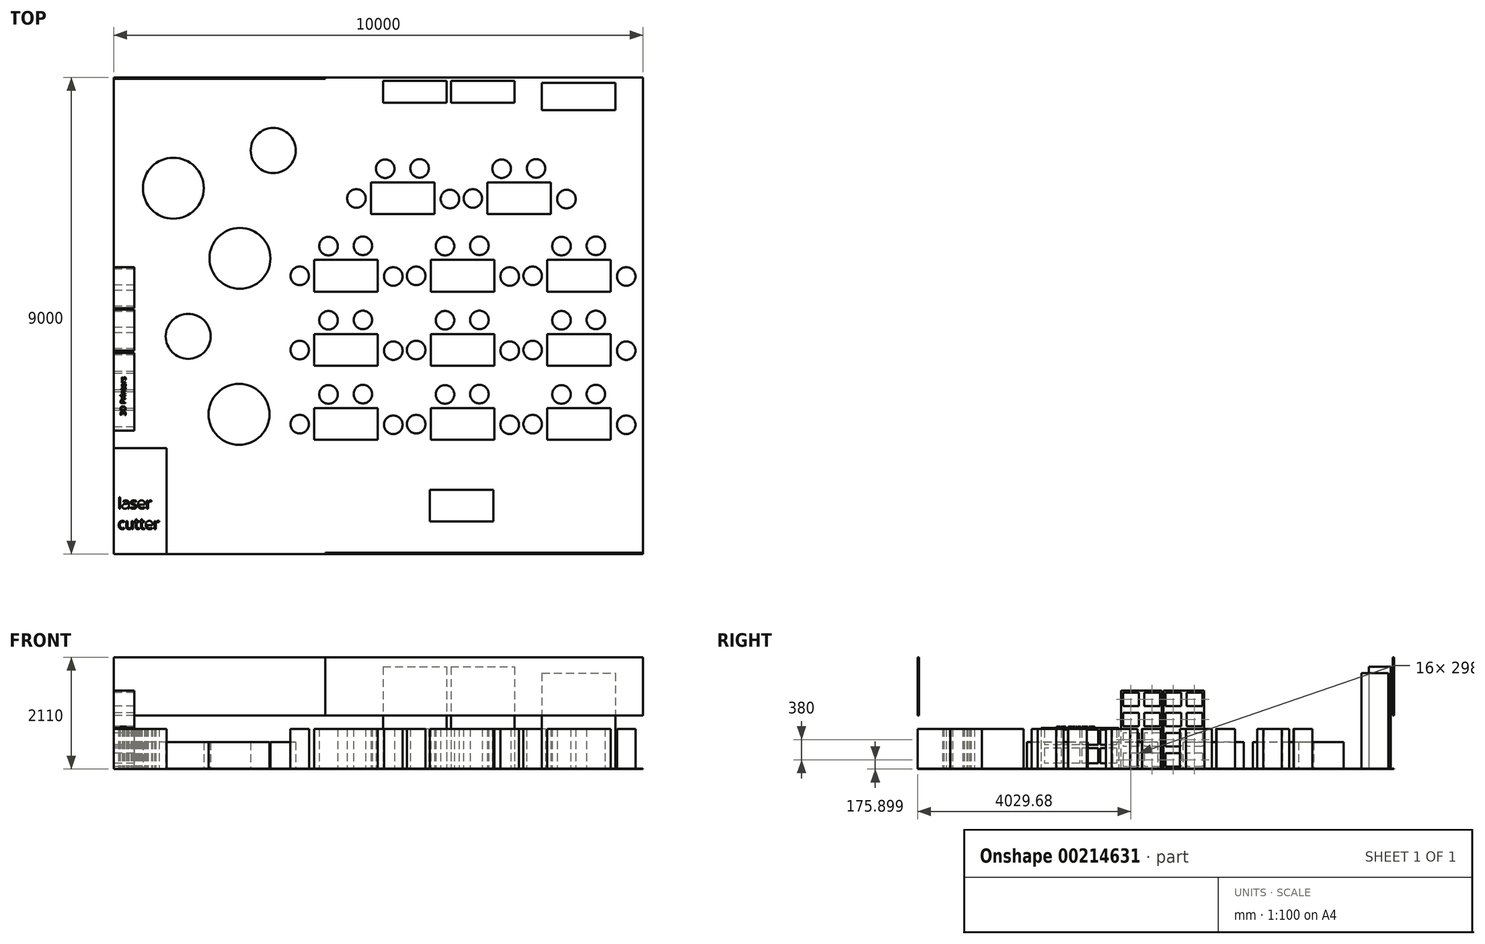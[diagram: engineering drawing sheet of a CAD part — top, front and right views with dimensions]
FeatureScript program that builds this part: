
annotation { "Feature Type Name" : "Feature", "Feature Type Description" : "" }
export const myFeature = defineFeature(function(context is Context, id is Id, definition is map)
    precondition{}
    {
        {
            var Q0;
            Q0=qCreatedBy(makeId("Top.planeOp"),FACE);
            var sketch = newSketch(context, id + "F0", { "sketchPlane" : qUnion([Q0])});
            skLineSegment(sketch, "E0.bottom", {"start": v(-5000, 4500) * mm, "end": v(5000, 4500) * mm});
            skLineSegment(sketch, "E0.top", {"start": v(-5000, -4500) * mm, "end": v(5000, -4500) * mm});
            skLineSegment(sketch, "E0.left", {"start": v(-5000, 4500) * mm, "end": v(-5000, -4500) * mm});
            skLineSegment(sketch, "E0.right", {"start": v(5000, 4500) * mm, "end": v(5000, -4500) * mm});
            skSolve(sketch);
        }
        {
            var Q0;
            Q0=makeQuery(id+"F0.imprint","IMPRINT",FACE,{"disambiguationData":[TD([[makeQuery(id+"F0.imprint","IMPRINT",EDGE,{"derivedFrom":sQuery(id+"F0.wireOp",EDGE,"E0.bottom")}),-1.0]])]});
            extrude(context, id + "F1", {"entities" : qUnion([Q0]), "oppositeDirection" : true, "depth" : 10 * mm});
        }
        {
            var Q0;
            Q0=qCreatedBy(makeId("Top.planeOp"),FACE);
            var sketch = newSketch(context, id + "F2", { "sketchPlane" : qUnion([Q0])});
            skLineSegment(sketch, "E1.bottom", {"start": v(972.24, -3285.08) * mm, "end": v(2172.24, -3285.08) * mm});
            skLineSegment(sketch, "E1.top", {"start": v(972.24, -3885.08) * mm, "end": v(2172.24, -3885.08) * mm});
            skLineSegment(sketch, "E1.left", {"start": v(972.24, -3285.08) * mm, "end": v(972.24, -3885.08) * mm});
            skLineSegment(sketch, "E1.right", {"start": v(2172.24, -3285.08) * mm, "end": v(2172.24, -3885.08) * mm});
            skLineSegment(sketch, "E2.bottom", {"start": v(3189.93, -1743.91) * mm, "end": v(4389.93, -1743.91) * mm});
            skLineSegment(sketch, "E2.top", {"start": v(3189.93, -2343.91) * mm, "end": v(4389.93, -2343.91) * mm});
            skLineSegment(sketch, "E2.left", {"start": v(3189.93, -1743.91) * mm, "end": v(3189.93, -2343.91) * mm});
            skLineSegment(sketch, "E2.right", {"start": v(4389.93, -1743.91) * mm, "end": v(4389.93, -2343.91) * mm});
            skCircle(sketch, "E3", {"center": v(2914.35, -2047.3) * mm, "radius": 175 * mm});
            skCircle(sketch, "E4", {"center": v(4108.01, -1479.73) * mm, "radius": 175 * mm});
            skCircle(sketch, "E5", {"center": v(3458.52, -1485.58) * mm, "radius": 175 * mm});
            skCircle(sketch, "E6", {"center": v(4681.44, -2059) * mm, "radius": 175 * mm});
            skCircle(sketch, "E7.0.1.0", {"center": v(2914.35, -647.3) * mm, "radius": 175 * mm});
            skCircle(sketch, "E7.0.1.1", {"center": v(4681.44, -659) * mm, "radius": 175 * mm});
            skLineSegment(sketch, "E7.0.1.2", {"start": v(4389.93, -343.91) * mm, "end": v(4389.93, -943.91) * mm});
            skCircle(sketch, "E7.0.1.3", {"center": v(3458.52, -85.58) * mm, "radius": 175 * mm});
            skLineSegment(sketch, "E7.0.1.4", {"start": v(3189.93, -343.91) * mm, "end": v(3189.93, -943.91) * mm});
            skCircle(sketch, "E7.0.1.5", {"center": v(4108.01, -79.73) * mm, "radius": 175 * mm});
            skLineSegment(sketch, "E7.0.1.6", {"start": v(3189.93, -943.91) * mm, "end": v(4389.93, -943.91) * mm});
            skLineSegment(sketch, "E7.0.1.7", {"start": v(3189.93, -343.91) * mm, "end": v(4389.93, -343.91) * mm});
            skCircle(sketch, "E7.0.2.0", {"center": v(2914.35, 752.7) * mm, "radius": 175 * mm});
            skCircle(sketch, "E7.0.2.1", {"center": v(4681.44, 741) * mm, "radius": 175 * mm});
            skLineSegment(sketch, "E7.0.2.2", {"start": v(4389.93, 1056.09) * mm, "end": v(4389.93, 456.09) * mm});
            skCircle(sketch, "E7.0.2.3", {"center": v(3458.52, 1314.42) * mm, "radius": 175 * mm});
            skLineSegment(sketch, "E7.0.2.4", {"start": v(3189.93, 1056.09) * mm, "end": v(3189.93, 456.09) * mm});
            skCircle(sketch, "E7.0.2.5", {"center": v(4108.01, 1320.27) * mm, "radius": 175 * mm});
            skLineSegment(sketch, "E7.0.2.6", {"start": v(3189.93, 456.09) * mm, "end": v(4389.93, 456.09) * mm});
            skLineSegment(sketch, "E7.0.2.7", {"start": v(3189.93, 1056.09) * mm, "end": v(4389.93, 1056.09) * mm});
            skCircle(sketch, "E7.1.0.0", {"center": v(714.35, -2047.3) * mm, "radius": 175 * mm});
            skCircle(sketch, "E7.1.0.1", {"center": v(2481.44, -2059) * mm, "radius": 175 * mm});
            skLineSegment(sketch, "E7.1.0.2", {"start": v(2189.93, -1743.91) * mm, "end": v(2189.93, -2343.91) * mm});
            skCircle(sketch, "E7.1.0.3", {"center": v(1258.52, -1485.58) * mm, "radius": 175 * mm});
            skLineSegment(sketch, "E7.1.0.4", {"start": v(989.93, -1743.91) * mm, "end": v(989.93, -2343.91) * mm});
            skCircle(sketch, "E7.1.0.5", {"center": v(1908.01, -1479.73) * mm, "radius": 175 * mm});
            skLineSegment(sketch, "E7.1.0.6", {"start": v(989.93, -2343.91) * mm, "end": v(2189.93, -2343.91) * mm});
            skLineSegment(sketch, "E7.1.0.7", {"start": v(989.93, -1743.91) * mm, "end": v(2189.93, -1743.91) * mm});
            skCircle(sketch, "E7.1.1.0", {"center": v(714.35, -647.3) * mm, "radius": 175 * mm});
            skCircle(sketch, "E7.1.1.1", {"center": v(2481.44, -659) * mm, "radius": 175 * mm});
            skLineSegment(sketch, "E7.1.1.2", {"start": v(2189.93, -343.91) * mm, "end": v(2189.93, -943.91) * mm});
            skCircle(sketch, "E7.1.1.3", {"center": v(1258.52, -85.58) * mm, "radius": 175 * mm});
            skLineSegment(sketch, "E7.1.1.4", {"start": v(989.93, -343.91) * mm, "end": v(989.93, -943.91) * mm});
            skCircle(sketch, "E7.1.1.5", {"center": v(1908.01, -79.73) * mm, "radius": 175 * mm});
            skLineSegment(sketch, "E7.1.1.6", {"start": v(989.93, -943.91) * mm, "end": v(2189.93, -943.91) * mm});
            skLineSegment(sketch, "E7.1.1.7", {"start": v(989.93, -343.91) * mm, "end": v(2189.93, -343.91) * mm});
            skCircle(sketch, "E7.1.2.0", {"center": v(714.35, 752.7) * mm, "radius": 175 * mm});
            skCircle(sketch, "E7.1.2.1", {"center": v(2481.44, 741) * mm, "radius": 175 * mm});
            skLineSegment(sketch, "E7.1.2.2", {"start": v(2189.93, 1056.09) * mm, "end": v(2189.93, 456.09) * mm});
            skCircle(sketch, "E7.1.2.3", {"center": v(1258.52, 1314.42) * mm, "radius": 175 * mm});
            skLineSegment(sketch, "E7.1.2.4", {"start": v(989.93, 1056.09) * mm, "end": v(989.93, 456.09) * mm});
            skCircle(sketch, "E7.1.2.5", {"center": v(1908.01, 1320.27) * mm, "radius": 175 * mm});
            skLineSegment(sketch, "E7.1.2.6", {"start": v(989.93, 456.09) * mm, "end": v(2189.93, 456.09) * mm});
            skLineSegment(sketch, "E7.1.2.7", {"start": v(989.93, 1056.09) * mm, "end": v(2189.93, 1056.09) * mm});
            skCircle(sketch, "E7.2.0.0", {"center": v(-1485.65, -2047.3) * mm, "radius": 175 * mm});
            skCircle(sketch, "E7.2.0.1", {"center": v(281.44, -2059) * mm, "radius": 175 * mm});
            skLineSegment(sketch, "E7.2.0.2", {"start": v(-10.07, -1743.91) * mm, "end": v(-10.07, -2343.91) * mm});
            skCircle(sketch, "E7.2.0.3", {"center": v(-941.48, -1485.58) * mm, "radius": 175 * mm});
            skLineSegment(sketch, "E7.2.0.4", {"start": v(-1210.07, -1743.91) * mm, "end": v(-1210.07, -2343.91) * mm});
            skCircle(sketch, "E7.2.0.5", {"center": v(-291.99, -1479.73) * mm, "radius": 175 * mm});
            skLineSegment(sketch, "E7.2.0.6", {"start": v(-1210.07, -2343.91) * mm, "end": v(-10.07, -2343.91) * mm});
            skLineSegment(sketch, "E7.2.0.7", {"start": v(-1210.07, -1743.91) * mm, "end": v(-10.07, -1743.91) * mm});
            skCircle(sketch, "E7.2.1.0", {"center": v(-1485.65, -647.3) * mm, "radius": 175 * mm});
            skCircle(sketch, "E7.2.1.1", {"center": v(281.44, -659) * mm, "radius": 175 * mm});
            skLineSegment(sketch, "E7.2.1.2", {"start": v(-10.07, -343.91) * mm, "end": v(-10.07, -943.91) * mm});
            skCircle(sketch, "E7.2.1.3", {"center": v(-941.48, -85.58) * mm, "radius": 175 * mm});
            skLineSegment(sketch, "E7.2.1.4", {"start": v(-1210.07, -343.91) * mm, "end": v(-1210.07, -943.91) * mm});
            skCircle(sketch, "E7.2.1.5", {"center": v(-291.99, -79.73) * mm, "radius": 175 * mm});
            skLineSegment(sketch, "E7.2.1.6", {"start": v(-1210.07, -943.91) * mm, "end": v(-10.07, -943.91) * mm});
            skLineSegment(sketch, "E7.2.1.7", {"start": v(-1210.07, -343.91) * mm, "end": v(-10.07, -343.91) * mm});
            skCircle(sketch, "E7.2.2.0", {"center": v(-1485.65, 752.7) * mm, "radius": 175 * mm});
            skCircle(sketch, "E7.2.2.1", {"center": v(281.44, 741) * mm, "radius": 175 * mm});
            skLineSegment(sketch, "E7.2.2.2", {"start": v(-10.07, 1056.09) * mm, "end": v(-10.07, 456.09) * mm});
            skCircle(sketch, "E7.2.2.3", {"center": v(-941.48, 1314.42) * mm, "radius": 175 * mm});
            skLineSegment(sketch, "E7.2.2.4", {"start": v(-1210.07, 1056.09) * mm, "end": v(-1210.07, 456.09) * mm});
            skCircle(sketch, "E7.2.2.5", {"center": v(-291.99, 1320.27) * mm, "radius": 175 * mm});
            skLineSegment(sketch, "E7.2.2.6", {"start": v(-1210.07, 456.09) * mm, "end": v(-10.07, 456.09) * mm});
            skLineSegment(sketch, "E7.2.2.7", {"start": v(-1210.07, 1056.09) * mm, "end": v(-10.07, 1056.09) * mm});
            skLineSegment(sketch, "E7.direction1", {"start": v(3189.93, -2343.91) * mm, "end": v(989.93, -2343.91) * mm, "construction": true});
            skLineSegment(sketch, "E7.direction2", {"start": v(3189.93, -2343.91) * mm, "end": v(3189.93, -943.91) * mm, "construction": true});
            skCircle(sketch, "E8.1.2.0", {"center": v(1784.74, 2214.43) * mm, "radius": 175 * mm});
            skCircle(sketch, "E8.1.2.1", {"center": v(3551.83, 2202.73) * mm, "radius": 175 * mm});
            skLineSegment(sketch, "E8.1.2.2", {"start": v(3260.32, 2517.83) * mm, "end": v(3260.32, 1917.83) * mm});
            skCircle(sketch, "E8.1.2.3", {"center": v(2328.91, 2776.16) * mm, "radius": 175 * mm});
            skLineSegment(sketch, "E8.1.2.4", {"start": v(2060.32, 2517.83) * mm, "end": v(2060.32, 1917.83) * mm});
            skCircle(sketch, "E8.1.2.5", {"center": v(2978.4, 2782) * mm, "radius": 175 * mm});
            skLineSegment(sketch, "E8.1.2.6", {"start": v(2060.32, 1917.83) * mm, "end": v(3260.32, 1917.83) * mm});
            skLineSegment(sketch, "E8.1.2.7", {"start": v(2060.32, 2517.83) * mm, "end": v(3260.32, 2517.83) * mm});
            skCircle(sketch, "E8.2.2.0", {"center": v(-415.26, 2214.43) * mm, "radius": 175 * mm});
            skCircle(sketch, "E8.2.2.1", {"center": v(1351.83, 2202.73) * mm, "radius": 175 * mm});
            skLineSegment(sketch, "E8.2.2.2", {"start": v(1060.32, 2517.83) * mm, "end": v(1060.32, 1917.83) * mm});
            skCircle(sketch, "E8.2.2.3", {"center": v(128.91, 2776.16) * mm, "radius": 175 * mm});
            skLineSegment(sketch, "E8.2.2.4", {"start": v(-139.68, 2517.83) * mm, "end": v(-139.68, 1917.83) * mm});
            skCircle(sketch, "E8.2.2.5", {"center": v(778.4, 2782) * mm, "radius": 175 * mm});
            skLineSegment(sketch, "E8.2.2.6", {"start": v(-139.68, 1917.83) * mm, "end": v(1060.32, 1917.83) * mm});
            skLineSegment(sketch, "E8.2.2.7", {"start": v(-139.68, 2517.83) * mm, "end": v(1060.32, 2517.83) * mm});
            skSolve(sketch);
        }
        {
            var Q0;
            Q0 = qSketchRegion(id + "F2", true);
            extrude(context, id + "F3", {"entities" : qUnion([Q0]), "operationType" : NewBodyOperationType.ADD, "depth" : 750 * mm});
        }
        {
            var Q0;
            Q0=qCreatedBy(makeId("Front.planeOp"),FACE);
            cPlane(context, id + "F4", {"entities" : qUnion([Q0]), "cplaneType" : CPlaneType.OFFSET, "offset" : 4500 * mm, "width" : 150 * mm, "height" : 150 * mm});
        }
        {
            var Q0;
            Q0=qCreatedBy(id+"F4.planeOp",FACE);
            var sketch = newSketch(context, id + "F5", { "sketchPlane" : qUnion([Q0])});
            skLineSegment(sketch, "E9.bottom", {"start": v(-1000, 2100) * mm, "end": v(5000, 2100) * mm});
            skLineSegment(sketch, "E9.top", {"start": v(-1000, 1000) * mm, "end": v(5000, 1000) * mm});
            skLineSegment(sketch, "E9.left", {"start": v(-1000, 2100) * mm, "end": v(-1000, 1000) * mm});
            skLineSegment(sketch, "E9.right", {"start": v(5000, 2100) * mm, "end": v(5000, 1000) * mm});
            skSolve(sketch);
        }
        {
            var Q0;
            Q0 = qSketchRegion(id + "F5", true);
            extrude(context, id + "F6", {"entities" : qUnion([Q0]), "oppositeDirection" : true, "depth" : 25 * mm});
        }
        {
            var Q0;
            Q0=qCreatedBy(makeId("Front.planeOp"),FACE);
            cPlane(context, id + "F7", {"entities" : qUnion([Q0]), "cplaneType" : CPlaneType.OFFSET, "offset" : 4500 * mm, "oppositeDirection" : true, "width" : 150 * mm, "height" : 150 * mm});
        }
        {
            var Q0;
            Q0=qCreatedBy(makeId("Top.planeOp"),FACE);
            var sketch = newSketch(context, id + "F8", { "sketchPlane" : qUnion([Q0])});
            skLineSegment(sketch, "E10.bottom", {"start": v(86.82, 4433.97) * mm, "end": v(1286.82, 4433.97) * mm});
            skLineSegment(sketch, "E10.top", {"start": v(86.82, 4023.97) * mm, "end": v(1286.82, 4023.97) * mm});
            skLineSegment(sketch, "E10.left", {"start": v(86.82, 4433.97) * mm, "end": v(86.82, 4023.97) * mm});
            skLineSegment(sketch, "E10.right", {"start": v(1286.82, 4433.97) * mm, "end": v(1286.82, 4023.97) * mm});
            skLineSegment(sketch, "E11.bottom", {"start": v(1369.44, 4433.5) * mm, "end": v(2569.44, 4433.5) * mm});
            skLineSegment(sketch, "E11.top", {"start": v(1369.44, 4023.5) * mm, "end": v(2569.44, 4023.5) * mm});
            skLineSegment(sketch, "E11.left", {"start": v(1369.44, 4433.5) * mm, "end": v(1369.44, 4023.5) * mm});
            skLineSegment(sketch, "E11.right", {"start": v(2569.44, 4433.5) * mm, "end": v(2569.44, 4023.5) * mm});
            skSolve(sketch);
        }
        {
            var Q0;
            Q0 = qSketchRegion(id + "F8", true);
            extrude(context, id + "F9", {"entities" : qUnion([Q0]), "operationType" : NewBodyOperationType.ADD, "depth" : 1920 * mm});
        }
        {
            var Q0;
            Q0=qCreatedBy(makeId("Top.planeOp"),FACE);
            var sketch = newSketch(context, id + "F10", { "sketchPlane" : qUnion([Q0])});
            skLineSegment(sketch, "E12.bottom", {"start": v(3086.65, 3884.82) * mm, "end": v(4476.65, 3884.82) * mm});
            skLineSegment(sketch, "E12.top", {"start": v(3086.65, 4394.82) * mm, "end": v(4476.65, 4394.82) * mm});
            skLineSegment(sketch, "E12.left", {"start": v(3086.65, 3884.82) * mm, "end": v(3086.65, 4394.82) * mm});
            skLineSegment(sketch, "E12.right", {"start": v(4476.65, 3884.82) * mm, "end": v(4476.65, 4394.82) * mm});
            skSolve(sketch);
        }
        {
            var Q0;
            Q0 = qSketchRegion(id + "F10", true);
            extrude(context, id + "F11", {"entities" : qUnion([Q0]), "operationType" : NewBodyOperationType.ADD, "depth" : 1800 * mm});
        }
        {
            var Q0;
            Q0=qCreatedBy(id+"F7.planeOp",FACE);
            var sketch = newSketch(context, id + "F12", { "sketchPlane" : qUnion([Q0])});
            skLineSegment(sketch, "E13.bottom", {"start": v(-1000, 2100) * mm, "end": v(-5000, 2100) * mm});
            skLineSegment(sketch, "E13.top", {"start": v(-1000, 1000) * mm, "end": v(-5000, 1000) * mm});
            skLineSegment(sketch, "E13.left", {"start": v(-1000, 2100) * mm, "end": v(-1000, 1000) * mm});
            skLineSegment(sketch, "E13.right", {"start": v(-5000, 2100) * mm, "end": v(-5000, 1000) * mm});
            skSolve(sketch);
        }
        {
            var Q0;
            Q0 = qSketchRegion(id + "F12", true);
            extrude(context, id + "F13", {"entities" : qUnion([Q0]), "depth" : 25 * mm});
        }
        {
            var Q0;
            Q0=qCreatedBy(makeId("Right.planeOp"),FACE);
            cPlane(context, id + "F14", {"entities" : qUnion([Q0]), "cplaneType" : CPlaneType.OFFSET, "offset" : 5000 * mm, "oppositeDirection" : true, "width" : 150 * mm, "height" : 150 * mm});
        }
        {
            var Q0;
            Q0=qCreatedBy(id+"F14.planeOp",FACE);
            var sketch = newSketch(context, id + "F15", { "sketchPlane" : qUnion([Q0])});
            skLineSegment(sketch, "E14.bottom", {"start": v(114.49, 0) * mm, "end": v(-655.51, 0) * mm});
            skLineSegment(sketch, "E14.top", {"start": v(114.49, 1470) * mm, "end": v(-655.51, 1470) * mm});
            skLineSegment(sketch, "E14.left", {"start": v(114.49, 0) * mm, "end": v(114.49, 1470) * mm});
            skLineSegment(sketch, "E14.right", {"start": v(-655.51, 0) * mm, "end": v(-655.51, 1470) * mm});
            skLineSegment(sketch, "E15.bottom", {"start": v(78.75, 1432.72) * mm, "end": v(-219.39, 1432.72) * mm});
            skLineSegment(sketch, "E15.top", {"start": v(78.75, 1179.08) * mm, "end": v(-219.39, 1179.08) * mm});
            skLineSegment(sketch, "E15.left", {"start": v(78.75, 1432.72) * mm, "end": v(78.75, 1179.08) * mm});
            skLineSegment(sketch, "E15.right", {"start": v(-219.39, 1432.72) * mm, "end": v(-219.39, 1179.08) * mm});
            skLineSegment(sketch, "E16.0.1.0", {"start": v(78.75, 1052.72) * mm, "end": v(78.75, 799.08) * mm});
            skLineSegment(sketch, "E16.0.1.1", {"start": v(78.75, 799.08) * mm, "end": v(-219.39, 799.08) * mm});
            skLineSegment(sketch, "E16.0.1.2", {"start": v(78.75, 1052.72) * mm, "end": v(-219.39, 1052.72) * mm});
            skLineSegment(sketch, "E16.0.1.3", {"start": v(-219.39, 1052.72) * mm, "end": v(-219.39, 799.08) * mm});
            skLineSegment(sketch, "E16.0.2.0", {"start": v(78.75, 672.72) * mm, "end": v(78.75, 419.08) * mm});
            skLineSegment(sketch, "E16.0.2.1", {"start": v(78.75, 419.08) * mm, "end": v(-219.39, 419.08) * mm});
            skLineSegment(sketch, "E16.0.2.2", {"start": v(78.75, 672.72) * mm, "end": v(-219.39, 672.72) * mm});
            skLineSegment(sketch, "E16.0.2.3", {"start": v(-219.39, 672.72) * mm, "end": v(-219.39, 419.08) * mm});
            skLineSegment(sketch, "E16.0.3.0", {"start": v(78.75, 292.72) * mm, "end": v(78.75, 39.08) * mm});
            skLineSegment(sketch, "E16.0.3.1", {"start": v(78.75, 39.08) * mm, "end": v(-219.39, 39.08) * mm});
            skLineSegment(sketch, "E16.0.3.2", {"start": v(78.75, 292.72) * mm, "end": v(-219.39, 292.72) * mm});
            skLineSegment(sketch, "E16.0.3.3", {"start": v(-219.39, 292.72) * mm, "end": v(-219.39, 39.08) * mm});
            skLineSegment(sketch, "E16.1.0.0", {"start": v(-321.25, 1432.72) * mm, "end": v(-321.25, 1179.08) * mm});
            skLineSegment(sketch, "E16.1.0.1", {"start": v(-321.25, 1179.08) * mm, "end": v(-619.39, 1179.08) * mm});
            skLineSegment(sketch, "E16.1.0.2", {"start": v(-321.25, 1432.72) * mm, "end": v(-619.39, 1432.72) * mm});
            skLineSegment(sketch, "E16.1.0.3", {"start": v(-619.39, 1432.72) * mm, "end": v(-619.39, 1179.08) * mm});
            skLineSegment(sketch, "E16.1.1.0", {"start": v(-321.25, 1052.72) * mm, "end": v(-321.25, 799.08) * mm});
            skLineSegment(sketch, "E16.1.1.1", {"start": v(-321.25, 799.08) * mm, "end": v(-619.39, 799.08) * mm});
            skLineSegment(sketch, "E16.1.1.2", {"start": v(-321.25, 1052.72) * mm, "end": v(-619.39, 1052.72) * mm});
            skLineSegment(sketch, "E16.1.1.3", {"start": v(-619.39, 1052.72) * mm, "end": v(-619.39, 799.08) * mm});
            skLineSegment(sketch, "E16.1.2.0", {"start": v(-321.25, 672.72) * mm, "end": v(-321.25, 419.08) * mm});
            skLineSegment(sketch, "E16.1.2.1", {"start": v(-321.25, 419.08) * mm, "end": v(-619.39, 419.08) * mm});
            skLineSegment(sketch, "E16.1.2.2", {"start": v(-321.25, 672.72) * mm, "end": v(-619.39, 672.72) * mm});
            skLineSegment(sketch, "E16.1.2.3", {"start": v(-619.39, 672.72) * mm, "end": v(-619.39, 419.08) * mm});
            skLineSegment(sketch, "E16.1.3.0", {"start": v(-321.25, 292.72) * mm, "end": v(-321.25, 39.08) * mm});
            skLineSegment(sketch, "E16.1.3.1", {"start": v(-321.25, 39.08) * mm, "end": v(-619.39, 39.08) * mm});
            skLineSegment(sketch, "E16.1.3.2", {"start": v(-321.25, 292.72) * mm, "end": v(-619.39, 292.72) * mm});
            skLineSegment(sketch, "E16.1.3.3", {"start": v(-619.39, 292.72) * mm, "end": v(-619.39, 39.08) * mm});
            skLineSegment(sketch, "E16.direction1", {"start": v(-219.39, 1179.08) * mm, "end": v(-619.39, 1179.08) * mm, "construction": true});
            skLineSegment(sketch, "E16.direction2", {"start": v(-219.39, 1179.08) * mm, "end": v(-219.39, 799.08) * mm, "construction": true});
            skLineSegment(sketch, "E17.1.0.0", {"start": v(478.75, 1052.72) * mm, "end": v(180.61, 1052.72) * mm});
            skLineSegment(sketch, "E17.1.0.1", {"start": v(878.75, 419.08) * mm, "end": v(580.61, 419.08) * mm});
            skLineSegment(sketch, "E17.1.0.2", {"start": v(878.75, 672.72) * mm, "end": v(580.61, 672.72) * mm});
            skLineSegment(sketch, "E17.1.0.3", {"start": v(580.61, 672.72) * mm, "end": v(580.61, 419.08) * mm});
            skLineSegment(sketch, "E17.1.0.4", {"start": v(914.49, 0) * mm, "end": v(144.49, 0) * mm});
            skLineSegment(sketch, "E17.1.0.5", {"start": v(914.49, 1470) * mm, "end": v(144.49, 1470) * mm});
            skLineSegment(sketch, "E17.1.0.6", {"start": v(914.49, 0) * mm, "end": v(914.49, 1470) * mm});
            skLineSegment(sketch, "E17.1.0.7", {"start": v(580.61, 292.72) * mm, "end": v(580.61, 39.08) * mm});
            skLineSegment(sketch, "E17.1.0.8", {"start": v(180.61, 292.72) * mm, "end": v(180.61, 39.08) * mm});
            skLineSegment(sketch, "E17.1.0.9", {"start": v(478.75, 419.08) * mm, "end": v(180.61, 419.08) * mm});
            skLineSegment(sketch, "E17.1.0.10", {"start": v(580.61, 1179.08) * mm, "end": v(180.61, 1179.08) * mm, "construction": true});
            skLineSegment(sketch, "E17.1.0.11", {"start": v(478.75, 1432.72) * mm, "end": v(478.75, 1179.08) * mm});
            skLineSegment(sketch, "E17.1.0.12", {"start": v(144.49, 0) * mm, "end": v(144.49, 1470) * mm});
            skLineSegment(sketch, "E17.1.0.13", {"start": v(878.75, 1432.72) * mm, "end": v(580.61, 1432.72) * mm});
            skLineSegment(sketch, "E17.1.0.14", {"start": v(878.75, 1179.08) * mm, "end": v(580.61, 1179.08) * mm});
            skLineSegment(sketch, "E17.1.0.15", {"start": v(878.75, 1432.72) * mm, "end": v(878.75, 1179.08) * mm});
            skLineSegment(sketch, "E17.1.0.16", {"start": v(478.75, 292.72) * mm, "end": v(478.75, 39.08) * mm});
            skLineSegment(sketch, "E17.1.0.17", {"start": v(878.75, 292.72) * mm, "end": v(878.75, 39.08) * mm});
            skLineSegment(sketch, "E17.1.0.18", {"start": v(580.61, 1432.72) * mm, "end": v(580.61, 1179.08) * mm});
            skLineSegment(sketch, "E17.1.0.19", {"start": v(878.75, 1052.72) * mm, "end": v(878.75, 799.08) * mm});
            skLineSegment(sketch, "E17.1.0.20", {"start": v(878.75, 799.08) * mm, "end": v(580.61, 799.08) * mm});
            skLineSegment(sketch, "E17.1.0.21", {"start": v(878.75, 1052.72) * mm, "end": v(580.61, 1052.72) * mm});
            skLineSegment(sketch, "E17.1.0.22", {"start": v(878.75, 672.72) * mm, "end": v(878.75, 419.08) * mm});
            skLineSegment(sketch, "E17.1.0.23", {"start": v(180.61, 1052.72) * mm, "end": v(180.61, 799.08) * mm});
            skLineSegment(sketch, "E17.1.0.24", {"start": v(180.61, 1432.72) * mm, "end": v(180.61, 1179.08) * mm});
            skLineSegment(sketch, "E17.1.0.25", {"start": v(580.61, 1179.08) * mm, "end": v(580.61, 799.08) * mm, "construction": true});
            skLineSegment(sketch, "E17.1.0.26", {"start": v(478.75, 672.72) * mm, "end": v(180.61, 672.72) * mm});
            skLineSegment(sketch, "E17.1.0.27", {"start": v(478.75, 39.08) * mm, "end": v(180.61, 39.08) * mm});
            skLineSegment(sketch, "E17.1.0.28", {"start": v(878.75, 39.08) * mm, "end": v(580.61, 39.08) * mm});
            skLineSegment(sketch, "E17.1.0.29", {"start": v(478.75, 672.72) * mm, "end": v(478.75, 419.08) * mm});
            skLineSegment(sketch, "E17.1.0.30", {"start": v(478.75, 1052.72) * mm, "end": v(478.75, 799.08) * mm});
            skLineSegment(sketch, "E17.1.0.31", {"start": v(180.61, 672.72) * mm, "end": v(180.61, 419.08) * mm});
            skLineSegment(sketch, "E17.1.0.32", {"start": v(478.75, 1432.72) * mm, "end": v(180.61, 1432.72) * mm});
            skLineSegment(sketch, "E17.1.0.33", {"start": v(478.75, 292.72) * mm, "end": v(180.61, 292.72) * mm});
            skLineSegment(sketch, "E17.1.0.34", {"start": v(878.75, 292.72) * mm, "end": v(580.61, 292.72) * mm});
            skLineSegment(sketch, "E17.1.0.35", {"start": v(478.75, 799.08) * mm, "end": v(180.61, 799.08) * mm});
            skLineSegment(sketch, "E17.1.0.36", {"start": v(580.61, 1052.72) * mm, "end": v(580.61, 799.08) * mm});
            skLineSegment(sketch, "E17.1.0.37", {"start": v(478.75, 1179.08) * mm, "end": v(180.61, 1179.08) * mm});
            skLineSegment(sketch, "E17.direction1", {"start": v(-655.51, 0) * mm, "end": v(144.49, 0) * mm, "construction": true});
            skSolve(sketch);
        }
        {
            var Q0;
            Q0=makeQuery(id+"F15.imprint","IMPRINT",FACE,{"disambiguationData":[TD([[makeQuery(id+"F15.imprint","IMPRINT",EDGE,{"derivedFrom":sQuery(id+"F15.wireOp",EDGE,"E17.1.0.0")}),-1.0]])]});
            var Q1;
            Q1=makeQuery(id+"F15.imprint","IMPRINT",FACE,{"disambiguationData":[TD([[makeQuery(id+"F15.imprint","IMPRINT",EDGE,{"derivedFrom":sQuery(id+"F15.wireOp",EDGE,"E14.bottom")}),-1.0]])]});
            extrude(context, id + "F16", {"entities" : qUnion([Q0, Q1]), "operationType" : NewBodyOperationType.ADD, "depth" : 390 * mm});
        }
        {
            var Q0;
            Q0=qCreatedBy(makeId("Top.planeOp"),FACE);
            var sketch = newSketch(context, id + "F17", { "sketchPlane" : qUnion([Q0])});
            skCircle(sketch, "E18", {"center": v(-3872.68, 2408.01) * mm, "radius": 575 * mm});
            skCircle(sketch, "E19", {"center": v(-2614.89, 1084.02) * mm, "radius": 575 * mm});
            skCircle(sketch, "E20", {"center": v(-2631.44, -1861.87) * mm, "radius": 575 * mm});
            skCircle(sketch, "E21", {"center": v(-3591.33, -388.92) * mm, "radius": 425 * mm});
            skCircle(sketch, "E22", {"center": v(-1985.99, 3119.66) * mm, "radius": 425 * mm});
            skSolve(sketch);
        }
        {
            var Q0;
            Q0 = qSketchRegion(id + "F17", true);
            extrude(context, id + "F18", {"entities" : qUnion([Q0]), "operationType" : NewBodyOperationType.ADD, "depth" : 500 * mm});
        }
        {
            var Q0;
            Q0=makeQuery(id+"F1.opExtrude","CAP_FACE",FACE,{"disambiguationData":[OSD([sQuery(id+"F0.wireOp",EDGE,"E0.bottom"),sQuery(id+"F0.wireOp",EDGE,"E0.top"),sQuery(id+"F0.wireOp",EDGE,"E0.left"),sQuery(id+"F0.wireOp",EDGE,"E0.right")])],"isStart":true});
            var sketch = newSketch(context, id + "F19", { "sketchPlane" : qUnion([Q0])});
            skLineSegment(sketch, "E23.bottom", {"start": v(-5000, -4500) * mm, "end": v(-4000, -4500) * mm});
            skLineSegment(sketch, "E23.top", {"start": v(-5000, -2500) * mm, "end": v(-4000, -2500) * mm});
            skLineSegment(sketch, "E23.left", {"start": v(-5000, -4500) * mm, "end": v(-5000, -2500) * mm});
            skLineSegment(sketch, "E23.right", {"start": v(-4000, -4500) * mm, "end": v(-4000, -2500) * mm});
            skText(sketch, "E24", { "text": "laser\ncutter", "fontName": "OpenSans-Regular.ttf"});
            const initialGuessF19  = {"E24": [-4.92101, -3.64126, 1, 0, 0.20456]};
            skSetInitialGuess(sketch, initialGuessF19);
            skSolve(sketch);
        }
        {
            var Q0;
            Q0=makeQuery(id+"F19.imprint","IMPRINT",FACE,{"disambiguationData":[TD([[makeQuery(id+"F19.imprint","IMPRINT",EDGE,{"derivedFrom":sQuery(id+"F19.wireOp",EDGE,"E23.bottom")}),1.0]])]});
            extrude(context, id + "F20", {"entities" : qUnion([Q0]), "operationType" : NewBodyOperationType.ADD, "depth" : 750 * mm});
        }
        {
            var Q0;
            Q0=qCreatedBy(id+"F14.planeOp",FACE);
            var sketch = newSketch(context, id + "F21", { "sketchPlane" : qUnion([Q0])});
            skLineSegment(sketch, "E25.bottom", {"start": v(-700, 770) * mm, "end": v(-2170, 770) * mm});
            skLineSegment(sketch, "E25.top", {"start": v(-700, 0) * mm, "end": v(-2170, 0) * mm});
            skLineSegment(sketch, "E25.left", {"start": v(-700, 770) * mm, "end": v(-700, 0) * mm});
            skLineSegment(sketch, "E25.right", {"start": v(-2170, 770) * mm, "end": v(-2170, 0) * mm});
            skLineSegment(sketch, "E26.bottom", {"start": v(-739.92, 734.78) * mm, "end": v(-1051.76, 734.78) * mm});
            skLineSegment(sketch, "E26.top", {"start": v(-739.92, 452.65) * mm, "end": v(-1051.76, 452.65) * mm});
            skLineSegment(sketch, "E26.left", {"start": v(-739.92, 734.78) * mm, "end": v(-739.92, 452.65) * mm});
            skLineSegment(sketch, "E26.right", {"start": v(-1051.76, 734.78) * mm, "end": v(-1051.76, 452.65) * mm});
            skLineSegment(sketch, "E27.0.1.0", {"start": v(-739.92, 384.78) * mm, "end": v(-1051.76, 384.78) * mm});
            skLineSegment(sketch, "E27.0.1.1", {"start": v(-700, 420) * mm, "end": v(-700, -350) * mm});
            skLineSegment(sketch, "E27.0.1.2", {"start": v(-739.92, 102.65) * mm, "end": v(-1051.76, 102.65) * mm});
            skLineSegment(sketch, "E27.0.1.3", {"start": v(-739.92, 384.78) * mm, "end": v(-739.92, 102.65) * mm});
            skLineSegment(sketch, "E27.0.1.4", {"start": v(-1051.76, 384.78) * mm, "end": v(-1051.76, 102.65) * mm});
            skLineSegment(sketch, "E27.1.0.0", {"start": v(-1089.92, 734.78) * mm, "end": v(-1401.76, 734.78) * mm});
            skLineSegment(sketch, "E27.1.0.1", {"start": v(-1050, 770) * mm, "end": v(-1050, 0) * mm});
            skLineSegment(sketch, "E27.1.0.2", {"start": v(-1089.92, 452.65) * mm, "end": v(-1401.76, 452.65) * mm});
            skLineSegment(sketch, "E27.1.0.3", {"start": v(-1089.92, 734.78) * mm, "end": v(-1089.92, 452.65) * mm});
            skLineSegment(sketch, "E27.1.0.4", {"start": v(-1401.76, 734.78) * mm, "end": v(-1401.76, 452.65) * mm});
            skLineSegment(sketch, "E27.1.1.0", {"start": v(-1089.92, 384.78) * mm, "end": v(-1401.76, 384.78) * mm});
            skLineSegment(sketch, "E27.1.1.1", {"start": v(-1050, 420) * mm, "end": v(-1050, -350) * mm});
            skLineSegment(sketch, "E27.1.1.2", {"start": v(-1089.92, 102.65) * mm, "end": v(-1401.76, 102.65) * mm});
            skLineSegment(sketch, "E27.1.1.3", {"start": v(-1089.92, 384.78) * mm, "end": v(-1089.92, 102.65) * mm});
            skLineSegment(sketch, "E27.1.1.4", {"start": v(-1401.76, 384.78) * mm, "end": v(-1401.76, 102.65) * mm});
            skLineSegment(sketch, "E27.2.0.0", {"start": v(-1439.92, 734.78) * mm, "end": v(-1751.76, 734.78) * mm});
            skLineSegment(sketch, "E27.2.0.1", {"start": v(-1400, 770) * mm, "end": v(-1400, 0) * mm});
            skLineSegment(sketch, "E27.2.0.2", {"start": v(-1439.92, 452.65) * mm, "end": v(-1751.76, 452.65) * mm});
            skLineSegment(sketch, "E27.2.0.3", {"start": v(-1439.92, 734.78) * mm, "end": v(-1439.92, 452.65) * mm});
            skLineSegment(sketch, "E27.2.0.4", {"start": v(-1751.76, 734.78) * mm, "end": v(-1751.76, 452.65) * mm});
            skLineSegment(sketch, "E27.2.1.0", {"start": v(-1439.92, 384.78) * mm, "end": v(-1751.76, 384.78) * mm});
            skLineSegment(sketch, "E27.2.1.1", {"start": v(-1400, 420) * mm, "end": v(-1400, -350) * mm});
            skLineSegment(sketch, "E27.2.1.2", {"start": v(-1439.92, 102.65) * mm, "end": v(-1751.76, 102.65) * mm});
            skLineSegment(sketch, "E27.2.1.3", {"start": v(-1439.92, 384.78) * mm, "end": v(-1439.92, 102.65) * mm});
            skLineSegment(sketch, "E27.2.1.4", {"start": v(-1751.76, 384.78) * mm, "end": v(-1751.76, 102.65) * mm});
            skLineSegment(sketch, "E27.3.0.0", {"start": v(-1789.92, 734.78) * mm, "end": v(-2101.76, 734.78) * mm});
            skLineSegment(sketch, "E27.3.0.1", {"start": v(-1750, 770) * mm, "end": v(-1750, 0) * mm});
            skLineSegment(sketch, "E27.3.0.2", {"start": v(-1789.92, 452.65) * mm, "end": v(-2101.76, 452.65) * mm});
            skLineSegment(sketch, "E27.3.0.3", {"start": v(-1789.92, 734.78) * mm, "end": v(-1789.92, 452.65) * mm});
            skLineSegment(sketch, "E27.3.0.4", {"start": v(-2101.76, 734.78) * mm, "end": v(-2101.76, 452.65) * mm});
            skLineSegment(sketch, "E27.3.1.0", {"start": v(-1789.92, 384.78) * mm, "end": v(-2101.76, 384.78) * mm});
            skLineSegment(sketch, "E27.3.1.1", {"start": v(-1750, 420) * mm, "end": v(-1750, -350) * mm});
            skLineSegment(sketch, "E27.3.1.2", {"start": v(-1789.92, 102.65) * mm, "end": v(-2101.76, 102.65) * mm});
            skLineSegment(sketch, "E27.3.1.3", {"start": v(-1789.92, 384.78) * mm, "end": v(-1789.92, 102.65) * mm});
            skLineSegment(sketch, "E27.3.1.4", {"start": v(-2101.76, 384.78) * mm, "end": v(-2101.76, 102.65) * mm});
            skLineSegment(sketch, "E27.direction1", {"start": v(-700, 0) * mm, "end": v(-1050, 0) * mm, "construction": true});
            skLineSegment(sketch, "E27.direction2", {"start": v(-700, 0) * mm, "end": v(-700, -350) * mm, "construction": true});
            skSolve(sketch);
        }
        {
            var Q0;
            Q0 = qSketchRegion(id + "F21", true);
            extrude(context, id + "F22", {"entities" : qUnion([Q0]), "operationType" : NewBodyOperationType.ADD, "depth" : 390 * mm});
        }
        {
            var Q0;
            Q0=makeQuery(id+"F22.opExtrude","SWEPT_FACE",FACE,{"disambiguationData":[OSD([sQuery(id+"F21.wireOp",EDGE,"E25.bottom")])]});
            var sketch = newSketch(context, id + "F23", { "sketchPlane" : qUnion([Q0])});
            skText(sketch, "E28", { "text": "3D Printers", "fontName": "OpenSans-Regular.ttf"});
            const initialGuessF23  = {"E28": [-4.77215, -1.88192, 0, 1, 0.1]};
            skSetInitialGuess(sketch, initialGuessF23);
            skSolve(sketch);
        }
        {
            var Q0;
            Q0 = qSketchRegion(id + "F23", true);
            extrude(context, id + "F24", {"entities" : qUnion([Q0]), "operationType" : NewBodyOperationType.ADD, "depth" : 25 * mm});
        }
    });
